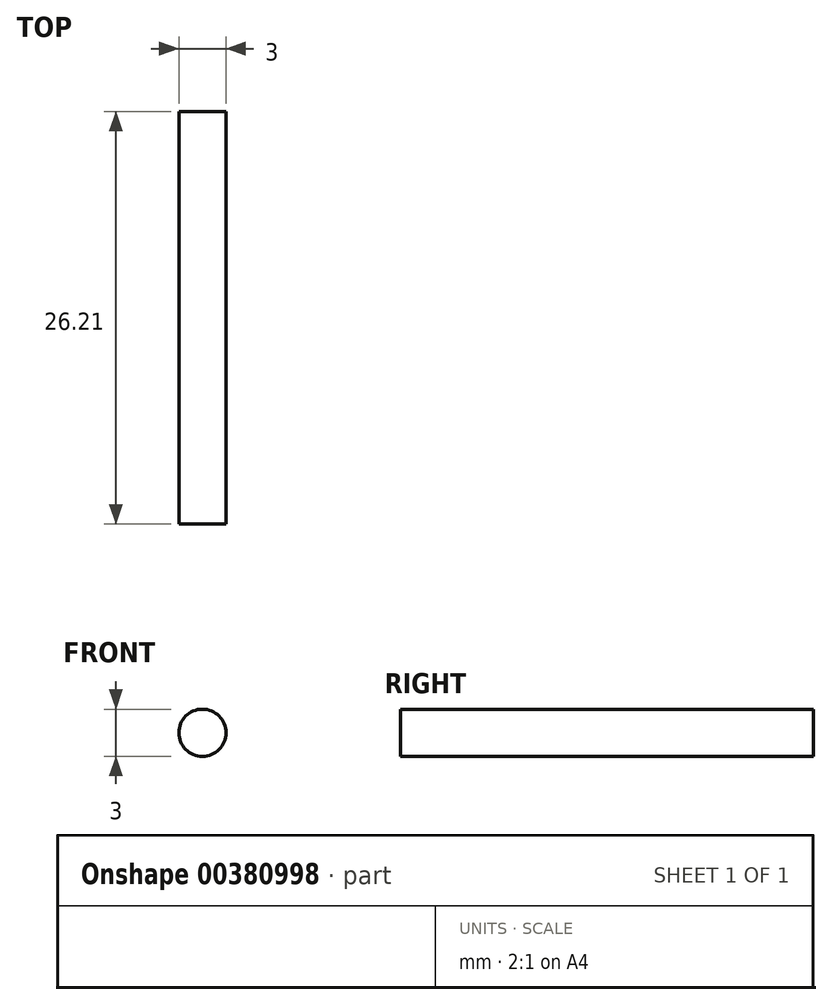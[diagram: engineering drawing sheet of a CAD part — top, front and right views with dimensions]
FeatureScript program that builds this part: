
annotation { "Feature Type Name" : "Feature", "Feature Type Description" : "" }
export const myFeature = defineFeature(function(context is Context, id is Id, definition is map)
    precondition{}
    {
        {
            var Q0;
            Q0=qCreatedBy(makeId("Front.planeOp"),FACE);
            var sketch = newSketch(context, id + "F0", { "sketchPlane" : qUnion([Q0])});
            skCircle(sketch, "E0", {"center": v(0, 0) * mm, "radius": 1.5 * mm});
            skSolve(sketch);
        }
        {
            var Q0;
            Q0=makeQuery(id+"F0.imprint","IMPRINT",FACE,{"disambiguationData":[TD([[makeQuery(id+"F0.imprint","IMPRINT",EDGE,{"derivedFrom":sQuery(id+"F0.wireOp",EDGE,"E0")}),1.0]])]});
            extrude(context, id + "F1", {"entities" : qUnion([Q0]), "oppositeDirection" : true, "depth" : 26.21 * mm});
        }
    });
